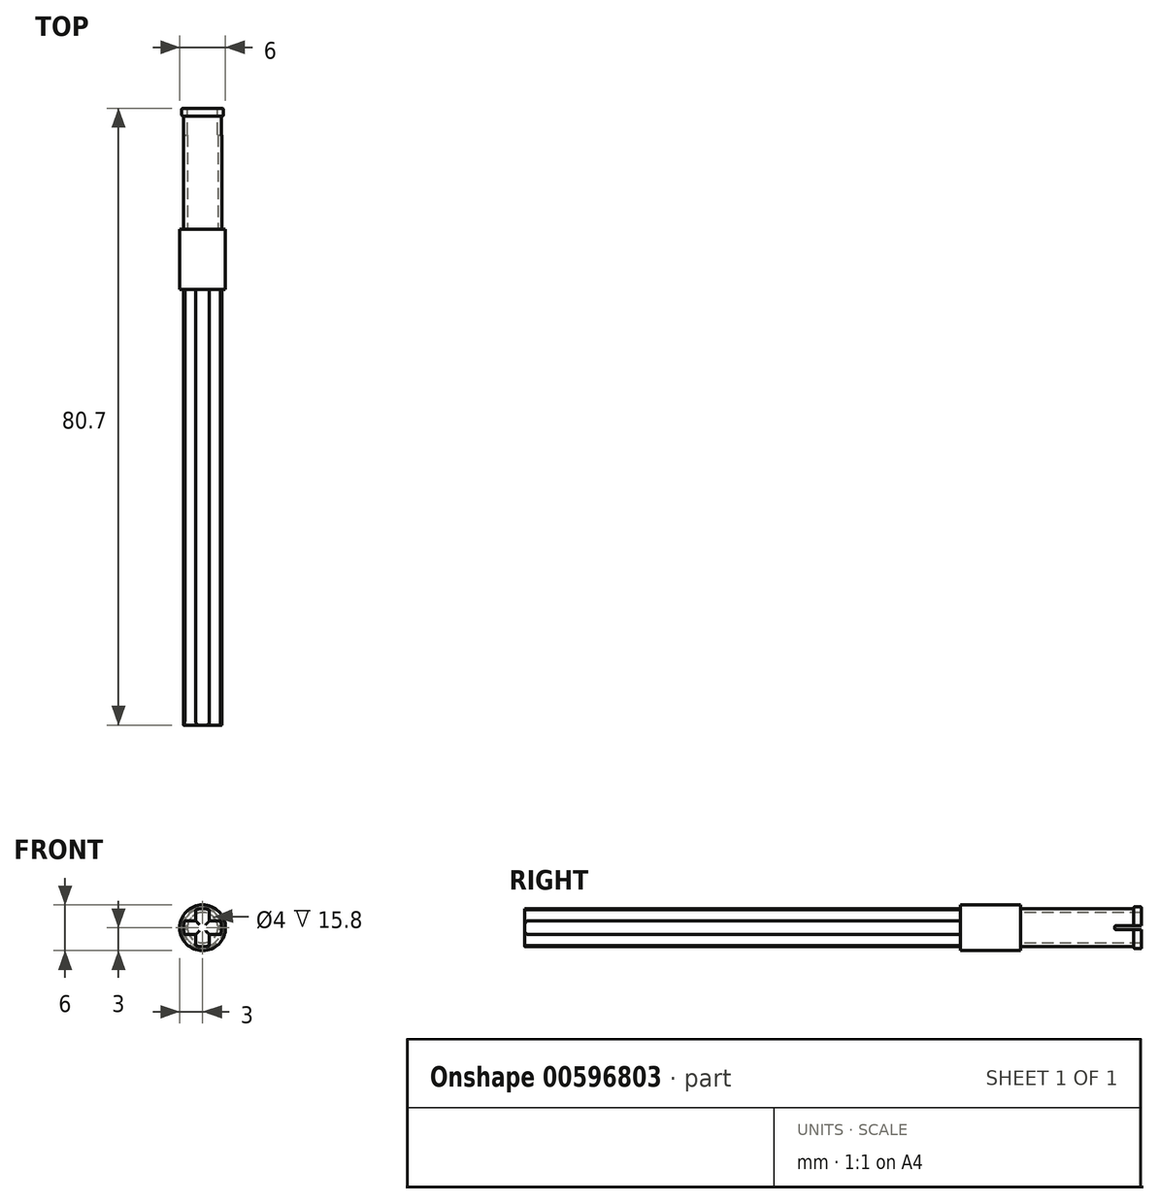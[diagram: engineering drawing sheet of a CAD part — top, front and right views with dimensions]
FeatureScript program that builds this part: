
annotation { "Feature Type Name" : "Feature", "Feature Type Description" : "" }
export const myFeature = defineFeature(function(context is Context, id is Id, definition is map)
    precondition{}
    {
        {
            var Q0;
            Q0=qCreatedBy(makeId("Front.planeOp"),FACE);
            var sketch = newSketch(context, id + "F0", { "sketchPlane" : qUnion([Q0])});
            skPoint(sketch, "E0.middle", {"position": v(0, 0) * mm});
            skLineSegment(sketch, "E1", {"start": v(-2.33, 0.9) * mm, "end": v(-0.9, 0.9) * mm});
            skLineSegment(sketch, "E2", {"start": v(-2.33, -0.9) * mm, "end": v(-0.9, -0.9) * mm});
            skLineSegment(sketch, "E3", {"start": v(-0.9, -2.33) * mm, "end": v(-0.9, -0.9) * mm});
            skLineSegment(sketch, "E4", {"start": v(0.9, -2.33) * mm, "end": v(0.9, -0.9) * mm});
            skLineSegment(sketch, "E5.trimOffspring", {"start": v(0.9, 0.9) * mm, "end": v(0.9, 2.33) * mm});
            skLineSegment(sketch, "E6.trimOffspring", {"start": v(0.9, 0.9) * mm, "end": v(2.33, 0.9) * mm});
            skLineSegment(sketch, "E7.trimOffspring", {"start": v(-0.9, 0.9) * mm, "end": v(-0.9, 2.33) * mm});
            skLineSegment(sketch, "E8.trimOffspring", {"start": v(0.9, -0.9) * mm, "end": v(2.33, -0.9) * mm});
            skArc(sketch, "E9", {"start": v(-0.9, -2.33) * mm, "mid": v(0, -2.5) * mm, "end": v(0.9, -2.33) * mm});
            skArc(sketch, "E10.trimOffspring", {"start": v(-2.33, 0.9) * mm, "mid": v(-2.5, 0) * mm, "end": v(-2.33, -0.9) * mm});
            skArc(sketch, "E11.trimOffspring", {"start": v(0.9, 2.33) * mm, "mid": v(0, 2.5) * mm, "end": v(-0.9, 2.33) * mm});
            skArc(sketch, "E12.trimOffspring", {"start": v(2.33, -0.9) * mm, "mid": v(2.5, 0) * mm, "end": v(2.33, 0.9) * mm});
            skSolve(sketch);
        }
        {
            var Q0;
            Q0=qSketchRegion(id+"F0",true);
            extrude(context, id + "F1", {"entities" : qUnion([Q0]), "endBound" : BoundingType.SYMMETRIC, "oppositeDirection" : true, "depth" : 57 * mm, "offsetDistance" : 25 * mm});
        }
        {
            var Q0;
            Q0=makeQuery(id+"F1.opExtrude","CAP_EDGE",EDGE,{"disambiguationData":[OSD([sQuery(id+"F0.wireOp",EDGE,"4f20bcb2-ca98-4e2b-a388-549ac28f8bc1.trimOffspring")])],"isStart":true});
            var Q1;
            Q1=makeQuery(id+"F1.opExtrude","CAP_EDGE",EDGE,{"disambiguationData":[OSD([sQuery(id+"F0.wireOp",EDGE,"E5.trimOffspring")])],"isStart":true});
            var Q2;
            Q2=makeQuery(id+"F1.opExtrude","CAP_EDGE",EDGE,{"disambiguationData":[OSD([sQuery(id+"F0.wireOp",EDGE,"E7.trimOffspring")])],"isStart":true});
            var Q3;
            Q3=makeQuery(id+"F1.opExtrude","CAP_EDGE",EDGE,{"disambiguationData":[OSD([sQuery(id+"F0.wireOp",EDGE,"E6.trimOffspring")])],"isStart":true});
            var Q4;
            Q4=makeQuery(id+"F1.opExtrude","CAP_EDGE",EDGE,{"disambiguationData":[OSD([sQuery(id+"F0.wireOp",EDGE,"155e961d-4448-4ca3-9a04-96ad712c6e00.trimOffspring")])],"isStart":true});
            var Q5;
            Q5=makeQuery(id+"F1.opExtrude","CAP_EDGE",EDGE,{"disambiguationData":[OSD([sQuery(id+"F0.wireOp",EDGE,"E8.trimOffspring")])],"isStart":true});
            var Q6;
            Q6=makeQuery(id+"F1.opExtrude","CAP_EDGE",EDGE,{"disambiguationData":[OSD([sQuery(id+"F0.wireOp",EDGE,"E4")])],"isStart":true});
            var Q7;
            Q7=makeQuery(id+"F1.opExtrude","CAP_EDGE",EDGE,{"disambiguationData":[OSD([sQuery(id+"F0.wireOp",EDGE,"ddc72866-e135-44d9-ad70-594a5f20fbf5.trimOffspring")])],"isStart":true});
            var Q8;
            Q8=makeQuery(id+"F1.opExtrude","CAP_EDGE",EDGE,{"disambiguationData":[OSD([sQuery(id+"F0.wireOp",EDGE,"E3")])],"isStart":true});
            var Q9;
            Q9=makeQuery(id+"F1.opExtrude","CAP_EDGE",EDGE,{"disambiguationData":[OSD([sQuery(id+"F0.wireOp",EDGE,"E2")])],"isStart":true});
            var Q10;
            Q10=makeQuery(id+"F1.opExtrude","CAP_EDGE",EDGE,{"disambiguationData":[OSD([sQuery(id+"F0.wireOp",EDGE,"LvV0EgKU-5q1w-1n0y-qFWI-tOOViCbsxCvn")])],"isStart":true});
            var Q11;
            Q11=makeQuery(id+"F1.opExtrude","CAP_EDGE",EDGE,{"disambiguationData":[OSD([sQuery(id+"F0.wireOp",EDGE,"E1")])],"isStart":true});
            fillet(context, id + "F2", {"entities" : qUnion([Q0, Q1, Q2, Q3, Q4, Q5, Q6, Q7, Q8, Q9, Q10, Q11]), "radius" : 0.5 * mm, "tangentPropagation" : true, "allowEdgeOverflow" : false});
        }
        {
            var Q0;
            Q0=makeQuery(id+"F1.opExtrude","CAP_FACE",FACE,{"disambiguationData":[OSD([sQuery(id+"F0.wireOp",EDGE,"E1"),sQuery(id+"F0.wireOp",EDGE,"E2"),sQuery(id+"F0.wireOp",EDGE,"E3"),sQuery(id+"F0.wireOp",EDGE,"E4"),sQuery(id+"F0.wireOp",EDGE,"E5.trimOffspring"),sQuery(id+"F0.wireOp",EDGE,"E6.trimOffspring"),sQuery(id+"F0.wireOp",EDGE,"E7.trimOffspring"),sQuery(id+"F0.wireOp",EDGE,"E8.trimOffspring"),sQuery(id+"F0.wireOp",EDGE,"E9"),sQuery(id+"F0.wireOp",EDGE,"E10.trimOffspring"),sQuery(id+"F0.wireOp",EDGE,"E11.trimOffspring"),sQuery(id+"F0.wireOp",EDGE,"E12.trimOffspring")])],"isStart":false});
            var sketch = newSketch(context, id + "F3", { "sketchPlane" : qUnion([Q0])});
            skCircle(sketch, "E13", {"center": v(0, 0) * mm, "radius": 3 * mm});
            skSolve(sketch);
        }
        {
            var Q0;
            Q0=makeQuery(id+"F3.imprint","IMPRINT",FACE,{"disambiguationData":[TD([[makeQuery(id+"F3.imprint","IMPRINT",EDGE,{"derivedFrom":makeQuery(id+"F1.opExtrude","CAP_EDGE",EDGE,{"disambiguationData":[OSD([sQuery(id+"F0.wireOp",EDGE,"E1")])],"isStart":false})}),1.0]])]});
            var Q1;
            Q1=makeQuery(id+"F3.imprint","IMPRINT",FACE,{"disambiguationData":[TD([[makeQuery(id+"F3.imprint","IMPRINT",EDGE,{"derivedFrom":sQuery(id+"F3.wireOp",EDGE,"E13")}),1.0]])]});
            extrude(context, id + "F4", {"entities" : qUnion([Q0, Q1]), "operationType" : NewBodyOperationType.ADD, "depth" : 7.9 * mm, "offsetDistance" : 25 * mm});
        }
        {
            var Q0;
            Q0=makeQuery(id+"F4.opExtrude","CAP_FACE",FACE,{"disambiguationData":[OSD([sQuery(id+"F3.wireOp",EDGE,"E13")])],"isStart":false});
            var sketch = newSketch(context, id + "F5", { "sketchPlane" : qUnion([Q0])});
            skCircle(sketch, "E14", {"center": v(0, 0) * mm, "radius": 2.5 * mm});
            skCircle(sketch, "E15", {"center": v(0, 0) * mm, "radius": 2 * mm});
            skSolve(sketch);
        }
        {
            var Q0;
            Q0=qSketchRegion(id+"F5",true);
            extrude(context, id + "F6", {"entities" : qUnion([Q0]), "operationType" : NewBodyOperationType.ADD, "depth" : 14.8 * mm, "offsetDistance" : 25 * mm});
        }
        {
            var Q0;
            Q0=makeQuery(id+"F6.opExtrude","CAP_FACE",FACE,{"disambiguationData":[OSD([sQuery(id+"F5.wireOp",EDGE,"E14"),sQuery(id+"F5.wireOp",EDGE,"E15")])],"isStart":false});
            var sketch = newSketch(context, id + "F7", { "sketchPlane" : qUnion([Q0])});
            skCircle(sketch, "E16", {"center": v(0, 0) * mm, "radius": 2.75 * mm});
            skSolve(sketch);
        }
        {
            var Q0;
            Q0=makeQuery(id+"F7.imprint","IMPRINT",FACE,{"disambiguationData":[TD([[makeQuery(id+"F7.imprint","IMPRINT",EDGE,{"derivedFrom":sQuery(id+"F7.wireOp",EDGE,"E16")}),1.0]])]});
            var Q1;
            Q1=makeQuery(id+"F7.imprint","IMPRINT",FACE,{"disambiguationData":[TD([[makeQuery(id+"F7.imprint","IMPRINT",EDGE,{"derivedFrom":makeQuery(id+"F6.opExtrude","CAP_EDGE",EDGE,{"disambiguationData":[OSD([sQuery(id+"F5.wireOp",EDGE,"E14")])],"isStart":false})}),1.0]])]});
            extrude(context, id + "F8", {"entities" : qUnion([Q0, Q1]), "operationType" : NewBodyOperationType.ADD, "depth" : 1 * mm, "offsetDistance" : 25 * mm});
        }
        {
            var Q0;
            Q0=makeQuery(id+"F8.opExtrude","CAP_FACE",FACE,{"disambiguationData":[OSD([sQuery(id+"F5.wireOp",EDGE,"E15"),sQuery(id+"F7.wireOp",EDGE,"E16")])],"isStart":false});
            var sketch = newSketch(context, id + "F9", { "sketchPlane" : qUnion([Q0])});
            skLineSegment(sketch, "E17", {"start": v(-1.98, 0.25) * mm, "end": v(-2.74, 0.25) * mm});
            skLineSegment(sketch, "E18", {"start": v(-2.74, -0.25) * mm, "end": v(-1.98, -0.25) * mm});
            skLineSegment(sketch, "E19", {"start": v(2.74, 0.25) * mm, "end": v(1.98, 0.25) * mm});
            skArc(sketch, "E20.0", {"start": v(1.98, -0.25) * mm, "mid": v(2, 0) * mm, "end": v(1.98, 0.25) * mm});
            skArc(sketch, "E21.0", {"start": v(-2.74, 0.25) * mm, "mid": v(-2.75, 0) * mm, "end": v(-2.74, -0.25) * mm});
            skLineSegment(sketch, "E22.trimOffspring", {"start": v(1.98, -0.25) * mm, "end": v(2.74, -0.25) * mm});
            skPoint(sketch, "E23.end.orphan", {"position": v(0, 0.25) * mm});
            skArc(sketch, "E24.trimOffspring", {"start": v(-1.98, 0.25) * mm, "mid": v(-2, 0) * mm, "end": v(-1.98, -0.25) * mm});
            skArc(sketch, "E25.trimOffspring", {"start": v(2.74, -0.25) * mm, "mid": v(2.75, 0) * mm, "end": v(2.74, 0.25) * mm});
            skSolve(sketch);
        }
        {
            var Q0;
            Q0=qSketchRegion(id+"F9",true);
            extrude(context, id + "F10", {"entities" : qUnion([Q0]), "operationType" : NewBodyOperationType.REMOVE, "oppositeDirection" : true, "depth" : 3.5 * mm, "offsetDistance" : 25 * mm});
        }
        {
            var Q0;
            Q0=makeQuery(id+"F10.boolean.opBoolean","COPY",EDGE,{"derivedFrom":makeQuery(id+"F10.opExtrude","CAP_EDGE",EDGE,{"disambiguationData":[OSD([sQuery(id+"F9.wireOp",EDGE,"E18")])],"isStart":false})});
            var Q1;
            Q1=makeQuery(id+"F10.boolean.opBoolean","COPY",EDGE,{"derivedFrom":makeQuery(id+"F10.opExtrude","CAP_EDGE",EDGE,{"disambiguationData":[OSD([sQuery(id+"F9.wireOp",EDGE,"E17")])],"isStart":false})});
            var Q2;
            Q2=makeQuery(id+"F10.boolean.opBoolean","COPY",EDGE,{"derivedFrom":makeQuery(id+"F10.opExtrude","CAP_EDGE",EDGE,{"disambiguationData":[OSD([sQuery(id+"F9.wireOp",EDGE,"E22.trimOffspring")])],"isStart":false})});
            var Q3;
            Q3=makeQuery(id+"F10.boolean.opBoolean","COPY",EDGE,{"derivedFrom":makeQuery(id+"F10.opExtrude","CAP_EDGE",EDGE,{"disambiguationData":[OSD([sQuery(id+"F9.wireOp",EDGE,"E19")])],"isStart":false})});
            fillet(context, id + "F11", {"entities" : qUnion([Q0, Q1, Q2, Q3]), "radius" : 0.15 * mm, "tangentPropagation" : true, "allowEdgeOverflow" : false});
        }
        {
            var Q0;
            {var subQ0=sQuery(id+"F7.wireOp",EDGE,"E16");Q0=makeQuery(id+"F10.boolean.opBoolean","SPLIT",EDGE,{"disambiguationData":[TD([makeQuery(id+"F10.opExtrude","SWEPT_FACE",FACE,{"disambiguationData":[OSD([sQuery(id+"F9.wireOp",EDGE,"E17")])]})])],"derivedFrom":makeQuery(id+"F8.opExtrude","CAP_EDGE",EDGE,{"disambiguationData":[OSD([subQ0])],"isStart":false})});}
            var Q1;
            {var subQ0=sQuery(id+"F7.wireOp",EDGE,"E16");Q1=makeQuery(id+"F10.boolean.opBoolean","SPLIT",EDGE,{"disambiguationData":[TD([makeQuery(id+"F10.opExtrude","SWEPT_FACE",FACE,{"disambiguationData":[OSD([sQuery(id+"F9.wireOp",EDGE,"E18")])]})])],"derivedFrom":makeQuery(id+"F8.opExtrude","CAP_EDGE",EDGE,{"disambiguationData":[OSD([subQ0])],"isStart":false})});}
            var Q2;
            {var subQ0=sQuery(id+"F7.wireOp",EDGE,"E16");Q2=makeQuery(id+"F10.boolean.opBoolean","SPLIT",EDGE,{"disambiguationData":[TD([makeQuery(id+"F10.opExtrude","SWEPT_FACE",FACE,{"disambiguationData":[OSD([sQuery(id+"F9.wireOp",EDGE,"E18")])]})])],"derivedFrom":makeQuery(id+"F8.opExtrude","CAP_EDGE",EDGE,{"disambiguationData":[OSD([subQ0])],"isStart":true})});}
            var Q3;
            {var subQ0=sQuery(id+"F7.wireOp",EDGE,"E16");Q3=makeQuery(id+"F10.boolean.opBoolean","SPLIT",EDGE,{"disambiguationData":[TD([makeQuery(id+"F10.opExtrude","SWEPT_FACE",FACE,{"disambiguationData":[OSD([sQuery(id+"F9.wireOp",EDGE,"E17")])]})])],"derivedFrom":makeQuery(id+"F8.opExtrude","CAP_EDGE",EDGE,{"disambiguationData":[OSD([subQ0])],"isStart":true})});}
            fillet(context, id + "F12", {"entities" : qUnion([Q0, Q1, Q2, Q3]), "radius" : 0.15 * mm, "tangentPropagation" : true, "allowEdgeOverflow" : false});
        }
    });
